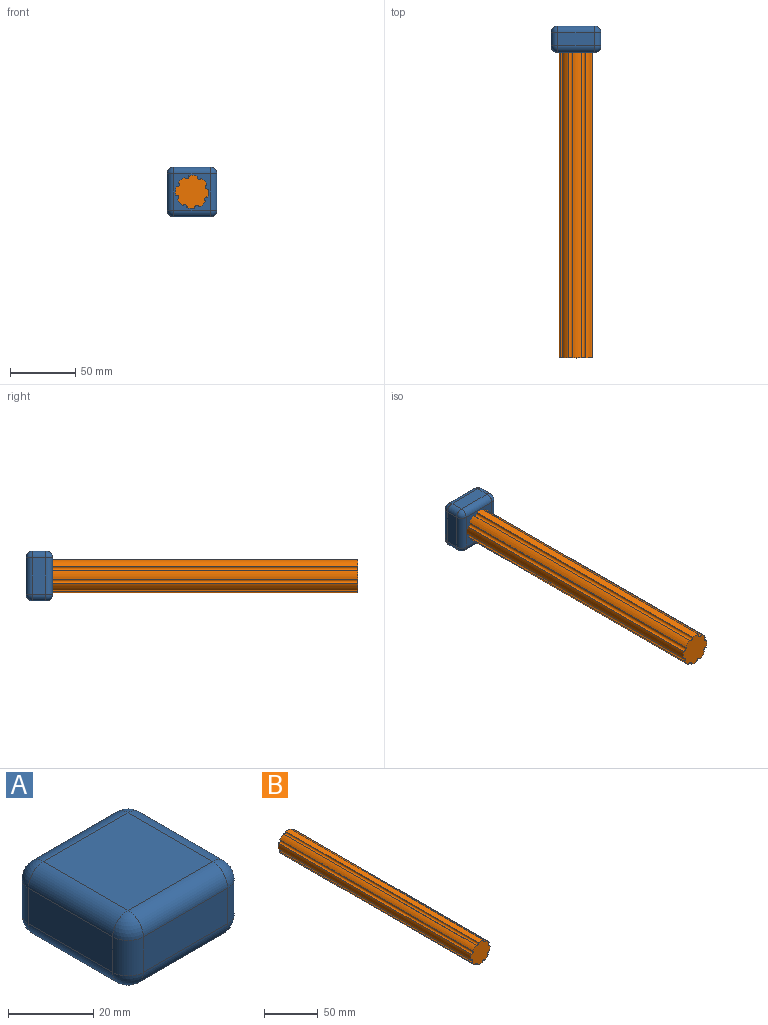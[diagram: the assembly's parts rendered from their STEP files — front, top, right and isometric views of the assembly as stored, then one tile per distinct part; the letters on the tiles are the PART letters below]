
ASSEMBLY  parts=2 mates=2
PART A: 26 faces, bbox 38.1x38.1x20.3 mm
  f0: plane 27.94x10.16mm, normal (0,1,0), area 283.9mm2, adj f14,f19,f22,f25
  f1: plane 27.94x10.16mm, normal (-1,0,0), area 283.9mm2, adj f11,f20,f21,f25
  f2: plane 27.94x10.16mm, normal (0,-1,0), area 283.9mm2, adj f6,f10,f11,f12
  f3: plane 27.94x10.16mm, normal (1,0,0), area 283.9mm2, adj f6,f9,f13,f14
  f4: plane 27.94x27.94mm, normal (0,0,1), area 780.6mm2, adj f9,f10,f19,f20
  f5: plane 27.94x27.94mm, normal (0,0,-1), area 780.6mm2, adj f12,f13,f21,f22
  f6: cylinder r=5.08mm len=10.16mm, axis (0,0,-1), area 81.1mm2, adj f2,f3,f7,f8
  f7: sphere r=5.08mm, area 40.5mm2, adj f6,f9,f10
  f8: sphere r=5.08mm, area 40.5mm2, adj f6,f12,f13
  f9: cylinder r=5.08mm len=27.94mm, axis (0,-1,0), area 223mm2, adj f3,f4,f7,f15
  f10: cylinder r=5.08mm len=27.94mm, axis (-1,0,0), area 223mm2, adj f2,f4,f7,f16
  f11: cylinder r=5.08mm len=10.16mm, axis (0,0,1), area 81.1mm2, adj f1,f2,f16,f17
  f12: cylinder r=5.08mm len=27.94mm, axis (1,0,0), area 223mm2, adj f2,f5,f8,f17
  f13: cylinder r=5.08mm len=27.94mm, axis (0,1,0), area 223mm2, adj f3,f5,f8,f18
  f14: cylinder r=5.08mm len=10.16mm, axis (0,0,1), area 81.1mm2, adj f0,f3,f15,f18
  f15: sphere r=5.08mm, area 40.5mm2, adj f9,f14,f19
  f16: sphere r=5.08mm, area 40.5mm2, adj f10,f11,f20
  f17: sphere r=5.08mm, area 40.5mm2, adj f11,f12,f21
  f18: sphere r=5.08mm, area 40.5mm2, adj f13,f14,f22
  f19: cylinder r=5.08mm len=27.94mm, axis (1,0,0), area 223mm2, adj f0,f4,f15,f23
  f20: cylinder r=5.08mm len=27.94mm, axis (0,1,0), area 223mm2, adj f1,f4,f16,f23
  f21: cylinder r=5.08mm len=27.94mm, axis (0,-1,0), area 223mm2, adj f1,f5,f17,f24
  f22: cylinder r=5.08mm len=27.94mm, axis (-1,0,0), area 223mm2, adj f0,f5,f18,f24
  f23: sphere r=5.08mm, area 40.5mm2, adj f19,f20,f25
  f24: sphere r=5.08mm, area 40.5mm2, adj f21,f22,f25
  f25: cylinder r=5.08mm len=10.16mm, axis (0,0,-1), area 81.1mm2, adj f0,f1,f23,f24
PART B: 18 faces, bbox 25.4x254x25.4 mm
  f0: cylinder r=1.78mm len=254mm, axis (0,-1,0), area 1355.5mm2, adj f1,f15,f16,f17
  f1: cylinder r=12.7mm len=254mm, axis (0,-1,0), area 1567.6mm2, adj f0,f2,f16,f17
  f2: cylinder r=1.78mm len=254mm, axis (0,-1,0), area 1355.5mm2, adj f1,f3,f16,f17
  f3: cylinder r=12.7mm len=254mm, axis (0,-1,0), area 1674mm2, adj f2,f4,f16,f17
  f4: cylinder r=1.78mm len=254mm, axis (0,-1,0), area 1355.5mm2, adj f3,f5,f16,f17
  f5: cylinder r=12.7mm len=254mm, axis (0,-1,0), area 1602.9mm2, adj f4,f6,f16,f17
  f6: cylinder r=1.78mm len=254mm, axis (0,-1,0), area 1355.5mm2, adj f5,f7,f16,f17
  f7: cylinder r=12.7mm len=254mm, axis (0,-1,0), area 1620.7mm2, adj f6,f8,f16,f17
  f8: cylinder r=1.78mm len=254mm, axis (0,-1,0), area 1355.5mm2, adj f7,f9,f16,f17
  f9: cylinder r=12.7mm len=254mm, axis (0,-1,0), area 1656.2mm2, adj f8,f10,f16,f17
  f10: cylinder r=1.78mm len=254mm, axis (0,-1,0), area 1355.5mm2, adj f9,f11,f16,f17
  f11: cylinder r=12.7mm len=254mm, axis (0,-1,0), area 1602.9mm2, adj f10,f12,f16,f17
  f12: cylinder r=1.78mm len=254mm, axis (0,-1,0), area 1355.5mm2, adj f11,f13,f16,f17
  f13: cylinder r=12.7mm len=254mm, axis (0,-1,0), area 1674mm2, adj f12,f14,f16,f17
  f14: cylinder r=1.78mm len=254mm, axis (0,-1,0), area 1355.5mm2, adj f13,f15,f16,f17
  f15: cylinder r=12.7mm len=254mm, axis (0,-1,0), area 1638.3mm2, adj f0,f14,f16,f17
  f16: plane 25.4x25.4mm, normal (0,1,0), area 468.2mm2, adj f0,f1,f2,f3,f4,f5,f6,f7
  f17: plane 25.4x25.4mm, normal (0,-1,0), area 468.2mm2, adj f0,f1,f2,f3,f4,f5,f6,f7
PLACE A rot(axis=(-1,0,0),90deg) t=(-38.4,679.31,-8.84)mm
PLACE B t=(5.79,445.63,67.34)mm fixed
MATE planar A.f4 <-> B.f1  axis (0,1,0) through (-81.74,699.63,37.03)mm
MATE slider B.f1 <-> A.f5  axis (0,1,0) through (-81.74,699.63,37.03)mm
